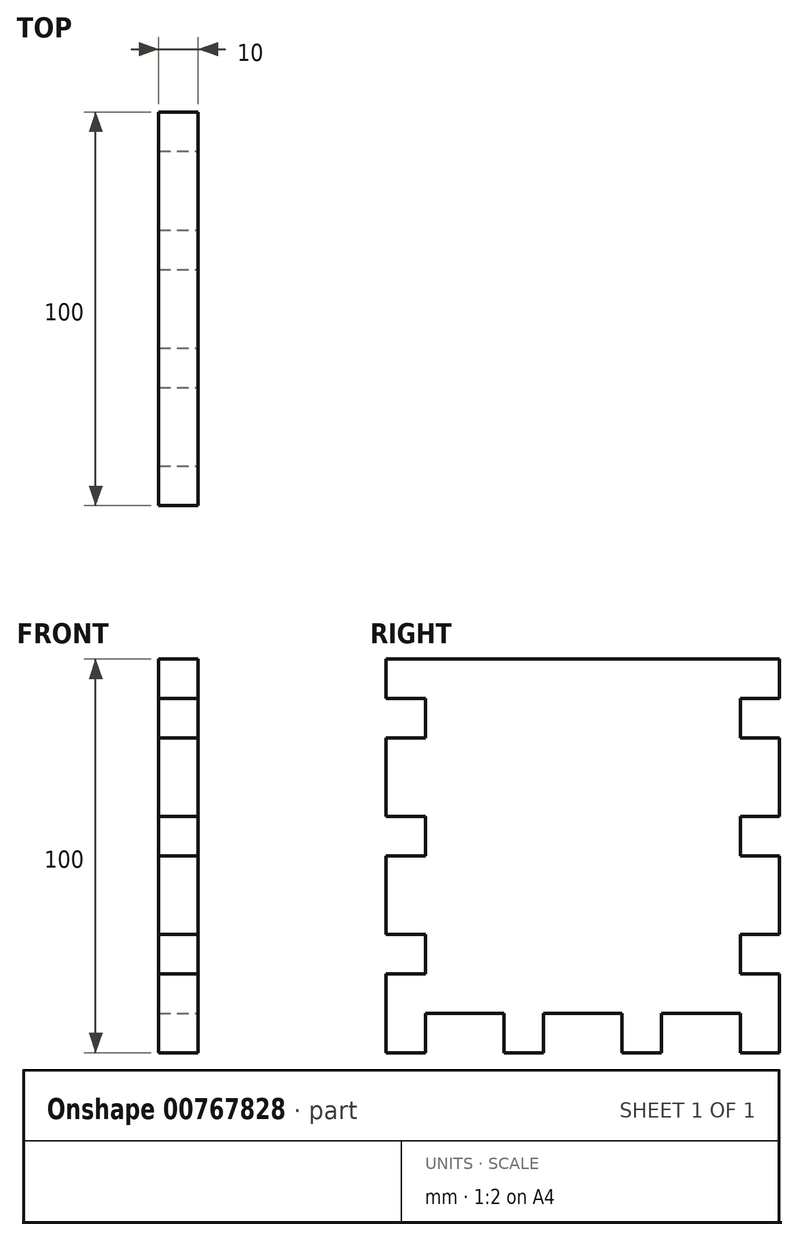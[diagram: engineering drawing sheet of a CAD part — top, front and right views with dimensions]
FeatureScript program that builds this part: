
annotation { "Feature Type Name" : "Feature", "Feature Type Description" : "" }
export const myFeature = defineFeature(function(context is Context, id is Id, definition is map)
    precondition{}
    {
        {
            var Q0;
            Q0=qCreatedBy(makeId("Right.planeOp"),FACE);
            var sketch = newSketch(context, id + "F0", { "sketchPlane" : qUnion([Q0])});
            skLineSegment(sketch, "E0.bottom", {"start": v(-38.87, 56.04) * mm, "end": v(61.13, 56.04) * mm});
            skLineSegment(sketch, "E0.top", {"start": v(-38.87, -43.96) * mm, "end": v(61.13, -43.96) * mm});
            skLineSegment(sketch, "E0.left", {"start": v(-38.87, 56.04) * mm, "end": v(-38.87, -43.96) * mm});
            skLineSegment(sketch, "E0.right", {"start": v(61.13, 56.04) * mm, "end": v(61.13, -43.96) * mm});
            skSolve(sketch);
        }
        {
            var Q0;
            Q0 = qSketchRegion(id + "F0", true);
            extrude(context, id + "F1", {"entities" : qUnion([Q0]), "depth" : 10 * mm, "offsetDistance" : 25 * mm});
        }
        {
            var Q0;
            Q0=makeQuery(id+"F1.opExtrude","CAP_FACE",FACE,{"disambiguationData":[OSD([sQuery(id+"F0.wireOp",EDGE,"E0.bottom"),sQuery(id+"F0.wireOp",EDGE,"E0.top"),sQuery(id+"F0.wireOp",EDGE,"E0.left"),sQuery(id+"F0.wireOp",EDGE,"E0.right")])],"isStart":false});
            var sketch = newSketch(context, id + "F2", { "sketchPlane" : qUnion([Q0])});
            skLineSegment(sketch, "E1.bottom", {"start": v(-28.87, -43.96) * mm, "end": v(-8.87, -43.96) * mm});
            skLineSegment(sketch, "E1.top", {"start": v(-28.87, -33.96) * mm, "end": v(-8.87, -33.96) * mm});
            skLineSegment(sketch, "E1.left", {"start": v(-28.87, -43.96) * mm, "end": v(-28.87, -33.96) * mm});
            skLineSegment(sketch, "E1.right", {"start": v(-8.87, -43.96) * mm, "end": v(-8.87, -33.96) * mm});
            skSolve(sketch);
        }
        {
            var Q0;
            Q0 = qSketchRegion(id + "F2", true);
            extrude(context, id + "F3", {"entities" : qUnion([Q0]), "operationType" : NewBodyOperationType.REMOVE, "oppositeDirection" : true, "depth" : 10 * mm, "offsetDistance" : 25 * mm});
        }
        {
            var Q0;
            Q0=makeQuery(id+"F1.opExtrude","CAP_FACE",FACE,{"disambiguationData":[OSD([sQuery(id+"F0.wireOp",EDGE,"E0.bottom"),sQuery(id+"F0.wireOp",EDGE,"E0.top"),sQuery(id+"F0.wireOp",EDGE,"E0.left"),sQuery(id+"F0.wireOp",EDGE,"E0.right")])],"isStart":false});
            var sketch = newSketch(context, id + "F4", { "sketchPlane" : qUnion([Q0])});
            skLineSegment(sketch, "E2.bottom", {"start": v(1.13, -43.96) * mm, "end": v(21.13, -43.96) * mm});
            skLineSegment(sketch, "E2.top", {"start": v(1.13, -33.96) * mm, "end": v(21.13, -33.96) * mm});
            skLineSegment(sketch, "E2.left", {"start": v(1.13, -43.96) * mm, "end": v(1.13, -33.96) * mm});
            skLineSegment(sketch, "E2.right", {"start": v(21.13, -43.96) * mm, "end": v(21.13, -33.96) * mm});
            skSolve(sketch);
        }
        {
            var Q0;
            Q0 = qSketchRegion(id + "F4", true);
            extrude(context, id + "F5", {"entities" : qUnion([Q0]), "operationType" : NewBodyOperationType.REMOVE, "oppositeDirection" : true, "depth" : 10 * mm, "offsetDistance" : 25 * mm});
        }
        {
            var Q0;
            Q0=makeQuery(id+"F1.opExtrude","CAP_FACE",FACE,{"disambiguationData":[OSD([sQuery(id+"F0.wireOp",EDGE,"E0.bottom"),sQuery(id+"F0.wireOp",EDGE,"E0.top"),sQuery(id+"F0.wireOp",EDGE,"E0.left"),sQuery(id+"F0.wireOp",EDGE,"E0.right")])],"isStart":false});
            var sketch = newSketch(context, id + "F6", { "sketchPlane" : qUnion([Q0])});
            skLineSegment(sketch, "E3.bottom", {"start": v(31.13, -43.96) * mm, "end": v(51.13, -43.96) * mm});
            skLineSegment(sketch, "E3.top", {"start": v(31.13, -33.96) * mm, "end": v(51.13, -33.96) * mm});
            skLineSegment(sketch, "E3.left", {"start": v(31.13, -43.96) * mm, "end": v(31.13, -33.96) * mm});
            skLineSegment(sketch, "E3.right", {"start": v(51.13, -43.96) * mm, "end": v(51.13, -33.96) * mm});
            skSolve(sketch);
        }
        {
            var Q0;
            Q0 = qSketchRegion(id + "F6", true);
            extrude(context, id + "F7", {"entities" : qUnion([Q0]), "operationType" : NewBodyOperationType.REMOVE, "oppositeDirection" : true, "depth" : 10 * mm, "offsetDistance" : 25 * mm});
        }
        {
            var Q0;
            Q0=makeQuery(id+"F1.opExtrude","CAP_FACE",FACE,{"disambiguationData":[OSD([sQuery(id+"F0.wireOp",EDGE,"E0.bottom"),sQuery(id+"F0.wireOp",EDGE,"E0.top"),sQuery(id+"F0.wireOp",EDGE,"E0.left"),sQuery(id+"F0.wireOp",EDGE,"E0.right")])],"isStart":false});
            var sketch = newSketch(context, id + "F8", { "sketchPlane" : qUnion([Q0])});
            skLineSegment(sketch, "E4.bottom", {"start": v(-38.87, -23.96) * mm, "end": v(-28.87, -23.96) * mm});
            skLineSegment(sketch, "E4.top", {"start": v(-38.87, -13.96) * mm, "end": v(-28.87, -13.96) * mm});
            skLineSegment(sketch, "E4.left", {"start": v(-38.87, -23.96) * mm, "end": v(-38.87, -13.96) * mm});
            skLineSegment(sketch, "E4.right", {"start": v(-28.87, -23.96) * mm, "end": v(-28.87, -13.96) * mm});
            skSolve(sketch);
        }
        {
            var Q0;
            Q0 = qSketchRegion(id + "F8", true);
            extrude(context, id + "F9", {"entities" : qUnion([Q0]), "operationType" : NewBodyOperationType.REMOVE, "oppositeDirection" : true, "depth" : 10 * mm, "offsetDistance" : 25 * mm});
        }
        {
            var Q0;
            Q0=makeQuery(id+"F1.opExtrude","CAP_FACE",FACE,{"disambiguationData":[OSD([sQuery(id+"F0.wireOp",EDGE,"E0.bottom"),sQuery(id+"F0.wireOp",EDGE,"E0.top"),sQuery(id+"F0.wireOp",EDGE,"E0.left"),sQuery(id+"F0.wireOp",EDGE,"E0.right")])],"isStart":false});
            var sketch = newSketch(context, id + "F10", { "sketchPlane" : qUnion([Q0])});
            skLineSegment(sketch, "E5.bottom", {"start": v(-38.87, 6.04) * mm, "end": v(-28.87, 6.04) * mm});
            skLineSegment(sketch, "E5.top", {"start": v(-38.87, 16.04) * mm, "end": v(-28.87, 16.04) * mm});
            skLineSegment(sketch, "E5.left", {"start": v(-38.87, 6.04) * mm, "end": v(-38.87, 16.04) * mm});
            skLineSegment(sketch, "E5.right", {"start": v(-28.87, 6.04) * mm, "end": v(-28.87, 16.04) * mm});
            skSolve(sketch);
        }
        {
            var Q0;
            Q0 = qSketchRegion(id + "F10", true);
            extrude(context, id + "F11", {"entities" : qUnion([Q0]), "operationType" : NewBodyOperationType.REMOVE, "oppositeDirection" : true, "depth" : 10 * mm, "offsetDistance" : 25 * mm});
        }
        {
            var Q0;
            Q0=makeQuery(id+"F1.opExtrude","CAP_FACE",FACE,{"disambiguationData":[OSD([sQuery(id+"F0.wireOp",EDGE,"E0.bottom"),sQuery(id+"F0.wireOp",EDGE,"E0.top"),sQuery(id+"F0.wireOp",EDGE,"E0.left"),sQuery(id+"F0.wireOp",EDGE,"E0.right")])],"isStart":false});
            var sketch = newSketch(context, id + "F12", { "sketchPlane" : qUnion([Q0])});
            skLineSegment(sketch, "E6.bottom", {"start": v(-38.87, 36.04) * mm, "end": v(-28.87, 36.04) * mm});
            skLineSegment(sketch, "E6.top", {"start": v(-38.87, 46.04) * mm, "end": v(-28.87, 46.04) * mm});
            skLineSegment(sketch, "E6.left", {"start": v(-38.87, 36.04) * mm, "end": v(-38.87, 46.04) * mm});
            skLineSegment(sketch, "E6.right", {"start": v(-28.87, 36.04) * mm, "end": v(-28.87, 46.04) * mm});
            skSolve(sketch);
        }
        {
            var Q0;
            Q0 = qSketchRegion(id + "F12", true);
            extrude(context, id + "F13", {"entities" : qUnion([Q0]), "operationType" : NewBodyOperationType.REMOVE, "oppositeDirection" : true, "depth" : 10 * mm, "offsetDistance" : 25 * mm});
        }
        {
            var Q0;
            Q0=makeQuery(id+"F1.opExtrude","CAP_FACE",FACE,{"disambiguationData":[OSD([sQuery(id+"F0.wireOp",EDGE,"E0.bottom"),sQuery(id+"F0.wireOp",EDGE,"E0.top"),sQuery(id+"F0.wireOp",EDGE,"E0.left"),sQuery(id+"F0.wireOp",EDGE,"E0.right")])],"isStart":false});
            var sketch = newSketch(context, id + "F14", { "sketchPlane" : qUnion([Q0])});
            skLineSegment(sketch, "E7.bottom", {"start": v(61.13, -23.96) * mm, "end": v(51.13, -23.96) * mm});
            skLineSegment(sketch, "E7.top", {"start": v(61.13, -13.96) * mm, "end": v(51.13, -13.96) * mm});
            skLineSegment(sketch, "E7.left", {"start": v(61.13, -23.96) * mm, "end": v(61.13, -13.96) * mm});
            skLineSegment(sketch, "E7.right", {"start": v(51.13, -23.96) * mm, "end": v(51.13, -13.96) * mm});
            skSolve(sketch);
        }
        {
            var Q0;
            Q0 = qSketchRegion(id + "F14", true);
            extrude(context, id + "F15", {"entities" : qUnion([Q0]), "operationType" : NewBodyOperationType.REMOVE, "oppositeDirection" : true, "depth" : 10 * mm, "offsetDistance" : 25 * mm});
        }
        {
            var Q0;
            Q0=makeQuery(id+"F1.opExtrude","CAP_FACE",FACE,{"disambiguationData":[OSD([sQuery(id+"F0.wireOp",EDGE,"E0.bottom"),sQuery(id+"F0.wireOp",EDGE,"E0.top"),sQuery(id+"F0.wireOp",EDGE,"E0.left"),sQuery(id+"F0.wireOp",EDGE,"E0.right")])],"isStart":false});
            var sketch = newSketch(context, id + "F16", { "sketchPlane" : qUnion([Q0])});
            skLineSegment(sketch, "E8.bottom", {"start": v(61.13, 6.04) * mm, "end": v(51.13, 6.04) * mm});
            skLineSegment(sketch, "E8.top", {"start": v(61.13, 16.04) * mm, "end": v(51.13, 16.04) * mm});
            skLineSegment(sketch, "E8.left", {"start": v(61.13, 6.04) * mm, "end": v(61.13, 16.04) * mm});
            skLineSegment(sketch, "E8.right", {"start": v(51.13, 6.04) * mm, "end": v(51.13, 16.04) * mm});
            skSolve(sketch);
        }
        {
            var Q0;
            Q0 = qSketchRegion(id + "F16", true);
            extrude(context, id + "F17", {"entities" : qUnion([Q0]), "operationType" : NewBodyOperationType.REMOVE, "oppositeDirection" : true, "depth" : 10 * mm, "offsetDistance" : 25 * mm});
        }
        {
            var Q0;
            Q0=makeQuery(id+"F1.opExtrude","CAP_FACE",FACE,{"disambiguationData":[OSD([sQuery(id+"F0.wireOp",EDGE,"E0.bottom"),sQuery(id+"F0.wireOp",EDGE,"E0.top"),sQuery(id+"F0.wireOp",EDGE,"E0.left"),sQuery(id+"F0.wireOp",EDGE,"E0.right")])],"isStart":false});
            var sketch = newSketch(context, id + "F18", { "sketchPlane" : qUnion([Q0])});
            skLineSegment(sketch, "E9.bottom", {"start": v(61.13, 36.04) * mm, "end": v(51.13, 36.04) * mm});
            skLineSegment(sketch, "E9.top", {"start": v(61.13, 46.04) * mm, "end": v(51.13, 46.04) * mm});
            skLineSegment(sketch, "E9.left", {"start": v(61.13, 36.04) * mm, "end": v(61.13, 46.04) * mm});
            skLineSegment(sketch, "E9.right", {"start": v(51.13, 36.04) * mm, "end": v(51.13, 46.04) * mm});
            skSolve(sketch);
        }
        {
            var Q0;
            Q0 = qSketchRegion(id + "F18", true);
            extrude(context, id + "F19", {"entities" : qUnion([Q0]), "operationType" : NewBodyOperationType.REMOVE, "oppositeDirection" : true, "depth" : 10 * mm, "offsetDistance" : 25 * mm});
        }
    });
